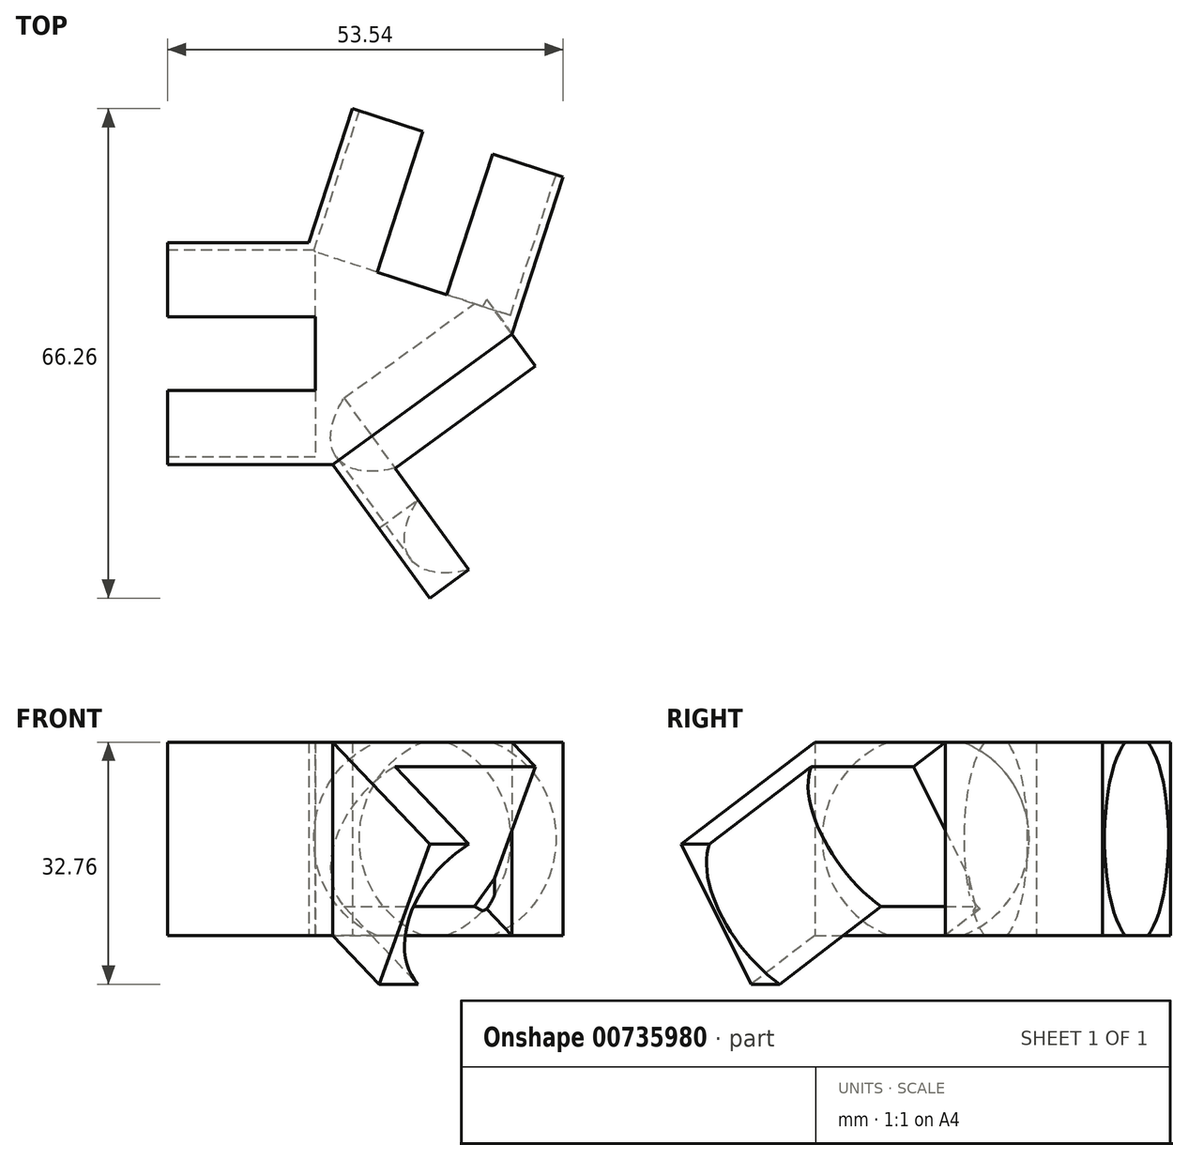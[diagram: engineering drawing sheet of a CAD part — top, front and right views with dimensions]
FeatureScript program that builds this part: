
annotation { "Feature Type Name" : "Feature", "Feature Type Description" : "" }
export const myFeature = defineFeature(function(context is Context, id is Id, definition is map)
    precondition{}
    {
        {
            var Q0;
            Q0=qCreatedBy(makeId("Top.planeOp"),FACE);
            var sketch = newSketch(context, id + "F0", { "sketchPlane" : qUnion([Q0])});
            skLineSegment(sketch, "E0.0", {"start": v(0, 0) * mm, "end": v(-30, 0) * mm});
            skLineSegment(sketch, "E0.4", {"start": v(9.27, 28.53) * mm, "end": v(0, 0) * mm});
            skLineSegment(sketch, "E1", {"start": v(0, 0) * mm, "end": v(17.63, -24.27) * mm});
            skLineSegment(sketch, "E2.0", {"start": v(-12.14, -8.82) * mm, "end": v(5.5, -33.09) * mm});
            skLineSegment(sketch, "E3.0", {"start": v(12.14, 8.82) * mm, "end": v(29.77, -15.45) * mm});
            skLineSegment(sketch, "E4.0", {"start": v(0, 15) * mm, "end": v(-30, 15) * mm});
            skLineSegment(sketch, "E5.0", {"start": v(0, -15) * mm, "end": v(-30, -15) * mm});
            skLineSegment(sketch, "E6.0", {"start": v(-5, 33.17) * mm, "end": v(-14.27, 4.64) * mm});
            skLineSegment(sketch, "E7.0", {"start": v(23.54, 23.9) * mm, "end": v(14.27, -4.64) * mm});
            skLineSegment(sketch, "E8", {"start": v(29.77, -15.45) * mm, "end": v(5.5, -33.09) * mm});
            skLineSegment(sketch, "E9", {"start": v(-30, -15) * mm, "end": v(-30, 15) * mm});
            skLineSegment(sketch, "E10", {"start": v(23.54, 23.9) * mm, "end": v(-5, 33.17) * mm});
            skSolve(sketch);
        }
        {
            var Q0;
            {var subQ8=sQuery(id+"F0.wireOp",EDGE,"E0.0");Q0=makeQuery(id+"F0.imprint","IMPRINT",FACE,{"disambiguationData":[TD([[makeQuery(id+"F0.imprint","IMPRINT",EDGE,{"derivedFrom":subQ8}),1.0]])]});}
            var Q1;
            {var subQ8=sQuery(id+"F0.wireOp",EDGE,"E0.4");Q1=makeQuery(id+"F0.imprint","IMPRINT",FACE,{"disambiguationData":[TD([[makeQuery(id+"F0.imprint","IMPRINT",EDGE,{"derivedFrom":subQ8}),1.0]])]});}
            var Q2;
            {var subQ7=sQuery(id+"F0.wireOp",EDGE,"E0.0");Q2=makeQuery(id+"F0.imprint","IMPRINT",FACE,{"disambiguationData":[TD([[makeQuery(id+"F0.imprint","IMPRINT",EDGE,{"derivedFrom":subQ7}),-1.0]])]});}
            extrude(context, id + "F1", {"entities" : qUnion([Q0, Q1, Q2]), "depth" : 40 * mm, "offsetDistance" : 25 * mm});
        }
        {
            var Q0;
            Q0=makeQuery(id+"F1.opExtrude","SWEPT_FACE",FACE,{"disambiguationData":[OSD([sQuery(id+"F0.wireOp",EDGE,"E3.0")])]});
            var sketch = newSketch(context, id + "F2", { "sketchPlane" : qUnion([Q0])});
            skLineSegment(sketch, "E11", {"start": v(-7.64, 40) * mm, "end": v(-30, 26.18) * mm});
            skLineSegment(sketch, "E12", {"start": v(-30, 26.18) * mm, "end": v(-30, 40) * mm});
            skLineSegment(sketch, "E13", {"start": v(-30, 40) * mm, "end": v(-7.64, 40) * mm});
            skPoint(sketch, "E14", {"position": v(-7.64, 40) * mm});
            skLineSegment(sketch, "E15", {"start": v(-18.3, 7.24) * mm, "end": v(-7.64, 13.82) * mm});
            skLineSegment(sketch, "E16", {"start": v(-30, 26.18) * mm, "end": v(-18.3, 7.24) * mm});
            skPoint(sketch, "E17.orphan", {"position": v(-30, 0) * mm});
            skSolve(sketch);
        }
        {
            var Q0;
            Q0=makeQuery(id+"F2.imprint","IMPRINT",FACE,{"disambiguationData":[TD([[makeQuery(id+"F2.imprint","IMPRINT",EDGE,{"derivedFrom":sQuery(id+"F2.wireOp",EDGE,"E11")}),-1.0]])]});
            var Q1;
            {var subQ4=sQuery(id+"F2.wireOp",EDGE,"E15");Q1=makeQuery(id+"F2.imprint","IMPRINT",FACE,{"disambiguationData":[TD([[makeQuery(id+"F2.imprint","IMPRINT",EDGE,{"derivedFrom":subQ4}),-1.0]])]});}
            extrude(context, id + "F3", {"entities" : qUnion([Q0, Q1]), "operationType" : NewBodyOperationType.REMOVE, "endBound" : BoundingType.UP_TO_NEXT, "oppositeDirection" : true, "depth" : 25 * mm, "offsetDistance" : 25 * mm});
        }
        {
            var Q0;
            Q0=makeQuery(id+"F1.opExtrude","CAP_FACE",FACE,{"disambiguationData":[OSD([sQuery(id+"F0.wireOp",EDGE,"E2.0"),sQuery(id+"F0.wireOp",EDGE,"E3.0"),sQuery(id+"F0.wireOp",EDGE,"E4.0"),sQuery(id+"F0.wireOp",EDGE,"E5.0"),sQuery(id+"F0.wireOp",EDGE,"E6.0"),sQuery(id+"F0.wireOp",EDGE,"E7.0"),sQuery(id+"F0.wireOp",EDGE,"E8"),sQuery(id+"F0.wireOp",EDGE,"E9"),sQuery(id+"F0.wireOp",EDGE,"E10")])],"isStart":true});
            var Q1;
            Q1=makeQuery(id+"F3.boolean.opBoolean","COPY",VERTEX,{"derivedFrom":makeQuery(id+"F3.opExtrude","CAP_VERTEX",VERTEX,{"disambiguationData":[OSD([sQuery(id+"F0.wireOp",EDGE,"E3.0"),sQuery(id+"F0.wireOp",EDGE,"E7.0"),sQuery(id+"F2.wireOp",EDGE,"E15")])],"isStart":true})});
            extrude(context, id + "F4", {"entities" : qUnion([Q0]), "operationType" : NewBodyOperationType.REMOVE, "endBound" : BoundingType.UP_TO_VERTEX, "oppositeDirection" : true, "depth" : 25 * mm, "endBoundEntityVertex" : qUnion([Q1]), "offsetDistance" : 25 * mm});
        }
        {
            var Q0;
            Q0=makeQuery(id+"F3.boolean.opBoolean","COPY",FACE,{"derivedFrom":makeQuery(id+"F3.opExtrude","SWEPT_FACE",FACE,{"disambiguationData":[OSD([sQuery(id+"F2.wireOp",EDGE,"E16")])]})});
            var sketch = newSketch(context, id + "F5", { "sketchPlane" : qUnion([Q0])});
            skLineSegment(sketch, "E18", {"start": v(-0.44, 40.9) * mm, "end": v(19.64, 9.38) * mm, "construction": true});
            skCircle(sketch, "E19", {"center": v(9.6, 25.14) * mm, "radius": 14 * mm});
            skSolve(sketch);
        }
        {
            var Q0;
            {var subQ0=sQuery(id+"F5.wireOp",EDGE,"E19");var subQ1=sQuery(id+"F2.wireOp",EDGE,"E16");var subQ8=makeQuery(id+"F3.boolean.opBoolean","COPY",EDGE,{"derivedFrom":makeQuery(id+"F3.opExtrude","SWEPT_EDGE",EDGE,{"disambiguationData":[OSD([sQuery(id+"F2.wireOp",EDGE,"E15"),subQ1])]})});var subQ9=makeQuery(id+"F5.imprint","INTERSECT",VERTEX,{"disambiguationData":[OD(0.0)],"derivedFrom":[subQ8,subQ0]});Q0=makeQuery(id+"F5.imprint","IMPRINT",FACE,{"disambiguationData":[TD([[makeQuery(id+"F5.imprint","IMPRINT",EDGE,{"disambiguationData":[TD([[subQ9,-1.0]])],"derivedFrom":subQ8}),1.0]])]});}
            var Q1;
            {var subQ0=sQuery(id+"F5.wireOp",EDGE,"E19");var subQ1=makeQuery(id+"F3.boolean.opBoolean","COPY",EDGE,{"derivedFrom":makeQuery(id+"F3.opExtrude","SWEPT_EDGE",EDGE,{"disambiguationData":[OSD([sQuery(id+"F2.wireOp",EDGE,"E15"),sQuery(id+"F2.wireOp",EDGE,"E16")])]})});var subQ2=makeQuery(id+"F5.imprint","INTERSECT",VERTEX,{"disambiguationData":[OD(0.0)],"derivedFrom":[subQ1,subQ0]});Q1=makeQuery(id+"F5.imprint","IMPRINT",FACE,{"disambiguationData":[TD([[makeQuery(id+"F5.imprint","IMPRINT",EDGE,{"disambiguationData":[TD([[subQ2,-1.0]])],"derivedFrom":subQ0}),1.0]])]});}
            extrude(context, id + "F6", {"entities" : qUnion([Q0, Q1]), "operationType" : NewBodyOperationType.REMOVE, "oppositeDirection" : true, "depth" : 20 * mm, "offsetDistance" : 25 * mm});
        }
        {
            var Q0;
            Q0=makeQuery(id+"F1.opExtrude","SWEPT_FACE",FACE,{"disambiguationData":[OSD([sQuery(id+"F0.wireOp",EDGE,"E10")])]});
            var sketch = newSketch(context, id + "F7", { "sketchPlane" : qUnion([Q0])});
            skLineSegment(sketch, "E20", {"start": v(-15, 40) * mm, "end": v(15, 13.82) * mm, "construction": true});
            skCircle(sketch, "E21", {"center": v(0, 26.9) * mm, "radius": 14 * mm});
            skSolve(sketch);
        }
        {
            var Q0;
            Q0 = qSketchRegion(id + "F7", true);
            extrude(context, id + "F8", {"entities" : qUnion([Q0]), "operationType" : NewBodyOperationType.REMOVE, "oppositeDirection" : true, "depth" : 20 * mm, "offsetDistance" : 25 * mm});
        }
        {
            var Q0;
            Q0=makeQuery(id+"F1.opExtrude","SWEPT_FACE",FACE,{"disambiguationData":[OSD([sQuery(id+"F0.wireOp",EDGE,"E9")])]});
            var sketch = newSketch(context, id + "F9", { "sketchPlane" : qUnion([Q0])});
            skLineSegment(sketch, "E22", {"start": v(-15, 40) * mm, "end": v(15, 13.82) * mm, "construction": true});
            skCircle(sketch, "E23", {"center": v(0, 26.9) * mm, "radius": 14 * mm});
            skSolve(sketch);
        }
        {
            var Q0;
            Q0 = qSketchRegion(id + "F9", true);
            extrude(context, id + "F10", {"entities" : qUnion([Q0]), "operationType" : NewBodyOperationType.REMOVE, "oppositeDirection" : true, "depth" : 20 * mm, "offsetDistance" : 25 * mm});
        }
    });
